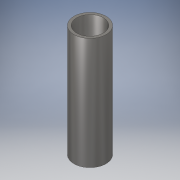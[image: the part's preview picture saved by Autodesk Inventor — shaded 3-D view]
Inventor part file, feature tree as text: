
AUTODESK INVENTOR PART (.ipt)
format: ipt  version: 2019 (Build 230136000, 136)  size: 102,400 bytes
history: native  units: mm
features: extrude x1, sketch x1
ambient origin geometry x8: Origin, YZ Plane, XZ Plane, XY Plane, X Axis, Y Axis, Z Axis, Center Point
bodies: Solid1 (feature_tree)
feature tree (2):
  extrude  "Extrusion1"  Depth=10.0mm
  sketch  "Sketch1"  dims[d0=12.0mm d1=10.0mm d2=42.0mm d3=0.0mm]
